# Revit family: RBA4110-993
name_source: partatom
category: Plumbing Fixtures
units: mm (PartAtom-declared; Revit-internal decimal feet)

## family parameters
Always vertical = Yes
Cut with Voids When Loaded = No
Part Type = Normal
Room Calculation Point = No
Round Connector Dimension = Use Diameter
Shared = Yes
Work Plane-Based = No

## types (1)
- RBA4110-993
    CW Connection = Yes
    Default Elevation = 0 mm  [stored 0 ft]
    Description = 900mm Straight Rail, 4 Star Handset, 2m Hose & Slider
    HW Connection = Yes
    Manufacturer = RBA Group
    Materials and Finishes = Chrome w/ Stainless Steel Satin Rail
    Model = RBA4110-993
    Modified Issue = 20201030.01
    URL = www.rba.com.au
    Vent Connection = Yes
    Waste Connection = Yes

note: [stored X ft] marks values corroborated as IEEE doubles in the binary element streams (Revit-internal decimal feet)

## geometry (parser evidence)
native form markers: Blend x2, Sweep x4
no freeform markers — native parametric forms only
